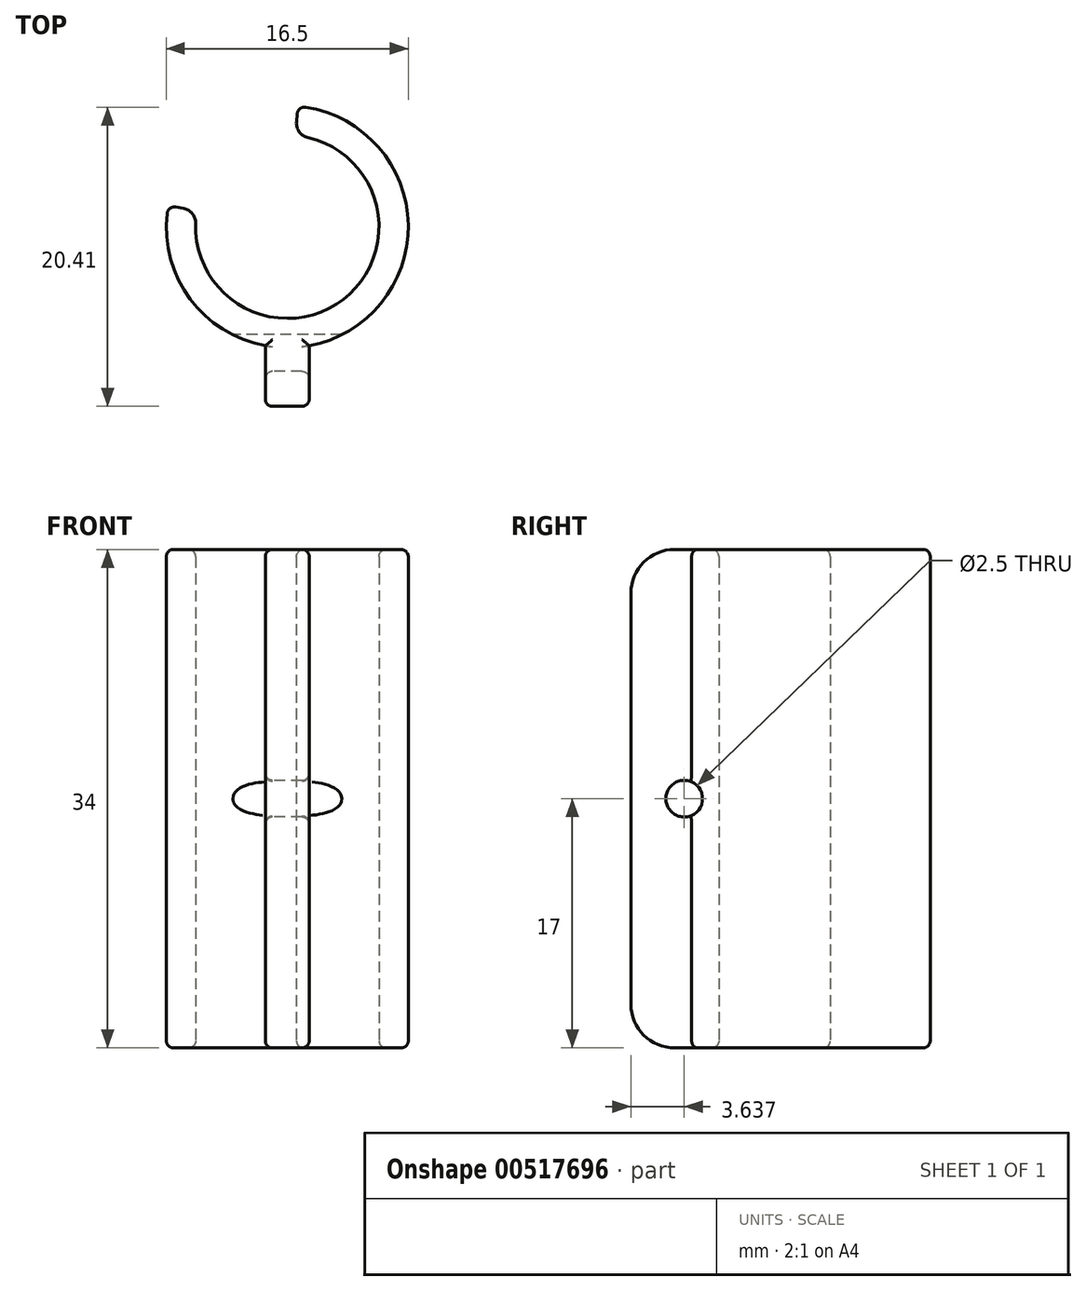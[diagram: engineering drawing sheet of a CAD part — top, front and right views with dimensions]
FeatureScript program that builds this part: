
annotation { "Feature Type Name" : "Feature", "Feature Type Description" : "" }
export const myFeature = defineFeature(function(context is Context, id is Id, definition is map)
    precondition{}
    {
        {
            var Q0;
            Q0=qCreatedBy(makeId("Top.planeOp"),FACE);
            var sketch = newSketch(context, id + "F0", { "sketchPlane" : qUnion([Q0])});
            skArc(sketch, "E0", {"start": v(-6.16, 1.09) * mm, "mid": v(3.8, -4.96) * mm, "end": v(0.54, 6.23) * mm});
            skArc(sketch, "E1", {"start": v(1.5, -8.11) * mm, "mid": v(8.24, 0.4) * mm, "end": v(0.72, 8.22) * mm});
            skLineSegment(sketch, "E2.top", {"start": v(-1.5, -12.25) * mm, "end": v(1.5, -12.25) * mm});
            skLineSegment(sketch, "E2.left", {"start": v(-1.5, -8.11) * mm, "end": v(-1.5, -12.25) * mm});
            skLineSegment(sketch, "E2.right", {"start": v(1.5, -8.11) * mm, "end": v(1.5, -12.25) * mm});
            skLineSegment(sketch, "E3", {"start": v(-6.16, 1.09) * mm, "end": v(-13.26, 2.34) * mm});
            skLineSegment(sketch, "E4", {"start": v(0.54, 6.23) * mm, "end": v(1.1, 12.56) * mm});
            skArc(sketch, "E5.trimOffspring", {"start": v(-8.12, 1.43) * mm, "mid": v(-6.78, -4.7) * mm, "end": v(-1.5, -8.11) * mm});
            skSolve(sketch);
        }
        {
            var Q0;
            {var subQ1=sQuery(id+"F0.wireOp",EDGE,"E0");Q0=makeQuery(id+"F0.imprint","IMPRINT",FACE,{"disambiguationData":[TD([[makeQuery(id+"F0.imprint","IMPRINT",EDGE,{"derivedFrom":subQ1}),-1.0]])]});}
            extrude(context, id + "F1", {"entities" : qUnion([Q0]), "depth" : 34 * mm, "offsetDistance" : 25 * mm});
        }
        {
            var Q0;
            Q0=qCreatedBy(makeId("Right.planeOp"),FACE);
            var sketch = newSketch(context, id + "F2", { "sketchPlane" : qUnion([Q0])});
            skLineSegment(sketch, "E6", {"start": v(20.08, 17) * mm, "end": v(-13.68, 17) * mm, "construction": true});
            skPoint(sketch, "E7", {"position": v(-8.61, 17) * mm});
            skCircle(sketch, "E8", {"center": v(-8.61, 17) * mm, "radius": 1.25 * mm});
            skSolve(sketch);
        }
        {
            var Q0;
            Q0 = qSketchRegion(id + "F2", true);
            extrude(context, id + "F3", {"entities" : qUnion([Q0]), "operationType" : NewBodyOperationType.REMOVE, "endBound" : BoundingType.THROUGH_ALL, "depth" : 25 * mm, "offsetDistance" : 25 * mm, "hasSecondDirection" : true, "secondDirectionBound" : SecondDirectionBoundingType.THROUGH_ALL, "secondDirectionOppositeDirection" : true, "secondDirectionDepth" : 25 * mm});
        }
        {
            var Q0;
            Q0=makeQuery(id+"F1.opExtrude","CAP_EDGE",EDGE,{"disambiguationData":[OSD([sQuery(id+"F0.wireOp",EDGE,"E2.top")])],"isStart":true});
            var Q1;
            Q1=makeQuery(id+"F1.opExtrude","CAP_EDGE",EDGE,{"disambiguationData":[OSD([sQuery(id+"F0.wireOp",EDGE,"E2.top")])],"isStart":false});
            fillet(context, id + "F4", {"entities" : qUnion([Q0, Q1]), "radius" : 3 * mm, "tangentPropagation" : true, "allowEdgeOverflow" : false});
        }
        {
            var Q0;
            Q0=makeQuery(id+"F1.opExtrude","CAP_EDGE",EDGE,{"disambiguationData":[OSD([sQuery(id+"F0.wireOp",EDGE,"E0")])],"isStart":false});
            var Q1;
            Q1=makeQuery(id+"F1.opExtrude","CAP_EDGE",EDGE,{"disambiguationData":[OSD([sQuery(id+"F0.wireOp",EDGE,"E0")])],"isStart":true});
            var Q2;
            Q2=makeQuery(id+"F1.opExtrude","CAP_EDGE",EDGE,{"disambiguationData":[OSD([sQuery(id+"F0.wireOp",EDGE,"E1")])],"isStart":true});
            var Q3;
            Q3=makeQuery(id+"F1.opExtrude","CAP_EDGE",EDGE,{"disambiguationData":[OSD([sQuery(id+"F0.wireOp",EDGE,"E5.trimOffspring")])],"isStart":true});
            var Q4;
            Q4=makeQuery(id+"F1.opExtrude","CAP_EDGE",EDGE,{"disambiguationData":[OSD([sQuery(id+"F0.wireOp",EDGE,"E2.right")])],"isStart":true});
            var Q5;
            Q5=makeQuery(id+"F4.opFillet","BLEND_EDGE",EDGE,{"blendedFrom":[makeQuery(id+"F1.opExtrude","CAP_EDGE",EDGE,{"disambiguationData":[OSD([sQuery(id+"F0.wireOp",EDGE,"E2.top")])],"isStart":true}),makeQuery(id+"F1.opExtrude","SWEPT_FACE",FACE,{"disambiguationData":[OSD([sQuery(id+"F0.wireOp",EDGE,"E2.right")])]})],"blendedInto":[makeQuery(id+"F1.opExtrude","SWEPT_FACE",FACE,{"disambiguationData":[OSD([sQuery(id+"F0.wireOp",EDGE,"E2.right")])]})]});
            var Q6;
            Q6=makeQuery(id+"F4.opFillet","BLEND_EDGE",EDGE,{"blendedFrom":[makeQuery(id+"F1.opExtrude","CAP_EDGE",EDGE,{"disambiguationData":[OSD([sQuery(id+"F0.wireOp",EDGE,"E2.top")])],"isStart":true}),makeQuery(id+"F1.opExtrude","SWEPT_FACE",FACE,{"disambiguationData":[OSD([sQuery(id+"F0.wireOp",EDGE,"E2.left")])]})],"blendedInto":[makeQuery(id+"F1.opExtrude","SWEPT_FACE",FACE,{"disambiguationData":[OSD([sQuery(id+"F0.wireOp",EDGE,"E2.left")])]})]});
            var Q7;
            Q7=makeQuery(id+"F1.opExtrude","CAP_EDGE",EDGE,{"disambiguationData":[OSD([sQuery(id+"F0.wireOp",EDGE,"E2.left")])],"isStart":true});
            var Q8;
            Q8=makeQuery(id+"F1.opExtrude","CAP_EDGE",EDGE,{"disambiguationData":[OSD([sQuery(id+"F0.wireOp",EDGE,"E1")])],"isStart":false});
            var Q9;
            Q9=makeQuery(id+"F1.opExtrude","CAP_EDGE",EDGE,{"disambiguationData":[OSD([sQuery(id+"F0.wireOp",EDGE,"E5.trimOffspring")])],"isStart":false});
            var Q10;
            Q10=makeQuery(id+"F1.opExtrude","CAP_EDGE",EDGE,{"disambiguationData":[OSD([sQuery(id+"F0.wireOp",EDGE,"E4")])],"isStart":false});
            var Q11;
            Q11=makeQuery(id+"F1.opExtrude","CAP_EDGE",EDGE,{"disambiguationData":[OSD([sQuery(id+"F0.wireOp",EDGE,"E3")])],"isStart":false});
            var Q12;
            Q12=makeQuery(id+"F1.opExtrude","CAP_EDGE",EDGE,{"disambiguationData":[OSD([sQuery(id+"F0.wireOp",EDGE,"E3")])],"isStart":true});
            var Q13;
            Q13=makeQuery(id+"F1.opExtrude","CAP_EDGE",EDGE,{"disambiguationData":[OSD([sQuery(id+"F0.wireOp",EDGE,"E4")])],"isStart":true});
            fillet(context, id + "F5", {"entities" : qUnion([Q0, Q1, Q2, Q3, Q4, Q5, Q6, Q7, Q8, Q9, Q10, Q11, Q12, Q13]), "radius" : .5 * mm, "tangentPropagation" : true, "allowEdgeOverflow" : false});
        }
        {
            var Q0;
            Q0=makeQuery(id+"F1.opExtrude","SWEPT_EDGE",EDGE,{"disambiguationData":[OSD([sQuery(id+"F0.wireOp",EDGE,"E3"),sQuery(id+"F0.wireOp",EDGE,"E5.trimOffspring")])]});
            var Q1;
            Q1=makeQuery(id+"F1.opExtrude","SWEPT_EDGE",EDGE,{"disambiguationData":[OSD([sQuery(id+"F0.wireOp",EDGE,"E1"),sQuery(id+"F0.wireOp",EDGE,"E4")])]});
            fillet(context, id + "F6", {"entities" : qUnion([Q0, Q1]), "radius" : .5 * mm, "tangentPropagation" : true, "allowEdgeOverflow" : false});
        }
        {
            var Q0;
            Q0=makeQuery(id+"F1.opExtrude","SWEPT_EDGE",EDGE,{"disambiguationData":[OSD([sQuery(id+"F0.wireOp",EDGE,"E0"),sQuery(id+"F0.wireOp",EDGE,"E3")])]});
            var Q1;
            Q1=makeQuery(id+"F1.opExtrude","SWEPT_EDGE",EDGE,{"disambiguationData":[OSD([sQuery(id+"F0.wireOp",EDGE,"E0"),sQuery(id+"F0.wireOp",EDGE,"E4")])]});
            fillet(context, id + "F7", {"entities" : qUnion([Q0, Q1]), "radius" : 1 * mm, "tangentPropagation" : true, "allowEdgeOverflow" : false});
        }
        {
            var Q0;
            Q0=makeQuery(id+"F3.boolean.opBoolean","INTERSECT",EDGE,{"derivedFrom":[makeQuery(id+"F1.opExtrude","SWEPT_FACE",FACE,{"disambiguationData":[OSD([sQuery(id+"F0.wireOp",EDGE,"E2.right")])]}),makeQuery(id+"F3.opExtrude","SWEPT_FACE",FACE,{"disambiguationData":[OSD([sQuery(id+"F2.wireOp",EDGE,"E8")])]})]});
            var Q1;
            Q1=makeQuery(id+"F3.boolean.opBoolean","INTERSECT",EDGE,{"derivedFrom":[makeQuery(id+"F1.opExtrude","SWEPT_FACE",FACE,{"disambiguationData":[OSD([sQuery(id+"F0.wireOp",EDGE,"E2.left")])]}),makeQuery(id+"F3.opExtrude","SWEPT_FACE",FACE,{"disambiguationData":[OSD([sQuery(id+"F2.wireOp",EDGE,"E8")])]})]});
            fillet(context, id + "F8", {"entities" : qUnion([Q0, Q1]), "radius" : .5 * mm, "tangentPropagation" : true, "allowEdgeOverflow" : false});
        }
    });
